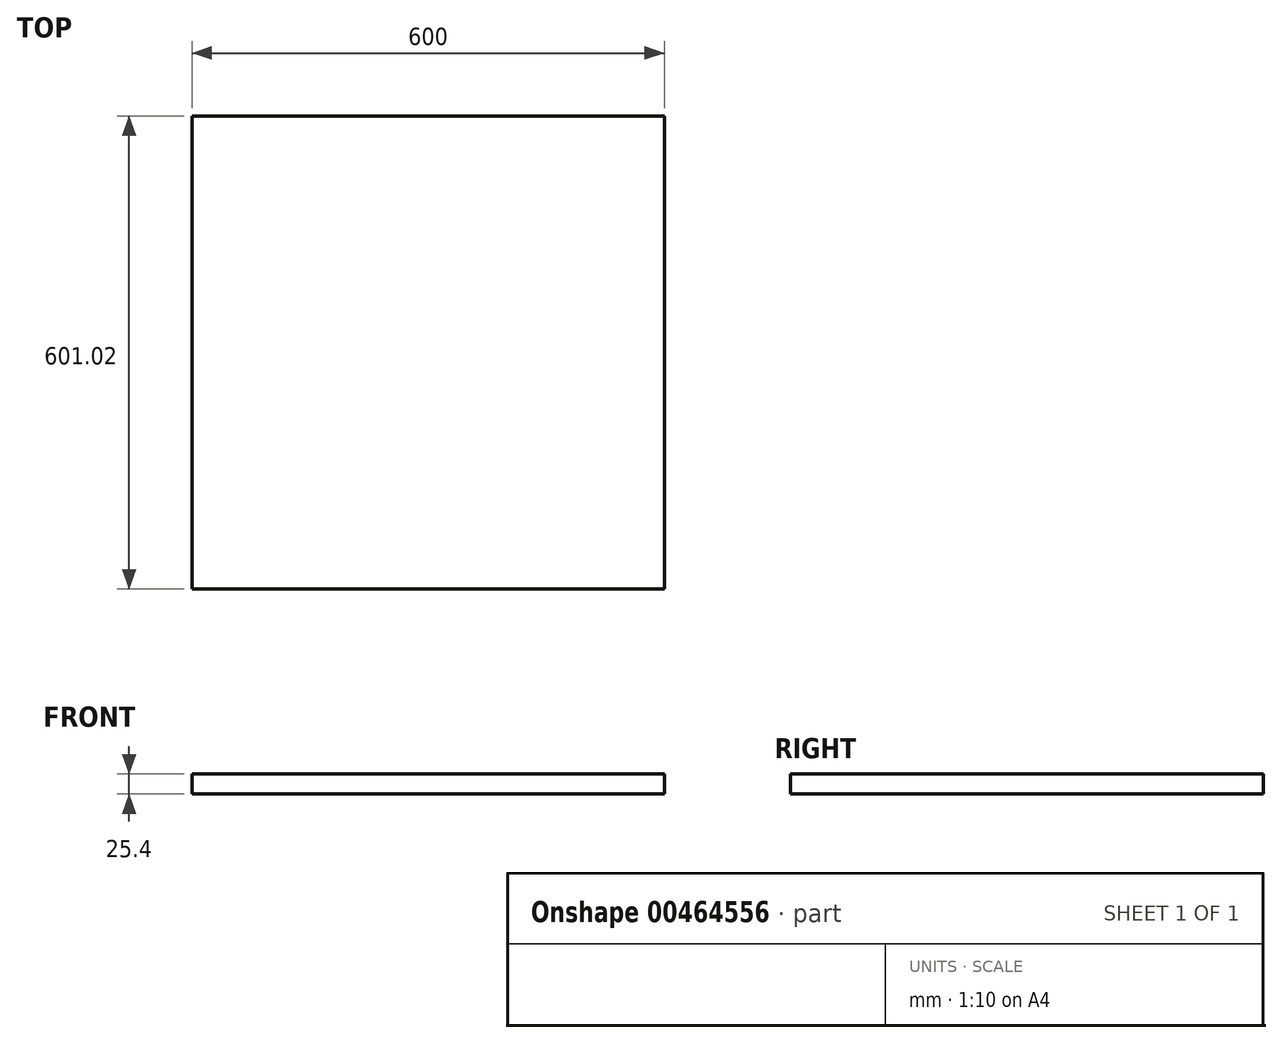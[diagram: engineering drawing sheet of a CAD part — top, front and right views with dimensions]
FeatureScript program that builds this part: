
annotation { "Feature Type Name" : "Feature", "Feature Type Description" : "" }
export const myFeature = defineFeature(function(context is Context, id is Id, definition is map)
    precondition{}
    {
        {
            var Q0;
            Q0=qCreatedBy(makeId("Top.planeOp"),FACE);
            var sketch = newSketch(context, id + "F0", { "sketchPlane" : qUnion([Q0])});
            skLineSegment(sketch, "E0.bottom", {"start": v(-300, -300.5) * mm, "end": v(300, -300.5) * mm});
            skLineSegment(sketch, "E0.top", {"start": v(-300, 300.5) * mm, "end": v(300, 300.5) * mm});
            skLineSegment(sketch, "E0.left", {"start": v(-300, -300.5) * mm, "end": v(-300, 300.5) * mm});
            skLineSegment(sketch, "E0.right", {"start": v(300, -300.5) * mm, "end": v(300, 300.5) * mm});
            skPoint(sketch, "E0.middle", {"position": v(0, 0) * mm});
            skSolve(sketch);
        }
        {
            var Q0;
            Q0=makeQuery(id+"F0.imprint","IMPRINT",FACE,{"disambiguationData":[TD([[makeQuery(id+"F0.imprint","IMPRINT",EDGE,{"derivedFrom":sQuery(id+"F0.wireOp",EDGE,"E0.bottom")}),1.0]])]});
            extrude(context, id + "F1", {"entities" : qUnion([Q0]), "depth" : 25.4 * mm});
        }
        {
            var Q0;
            Q0=makeQuery(id+"F1.opExtrude","CAP_FACE",FACE,{"disambiguationData":[OSD([sQuery(id+"F0.wireOp",EDGE,"E0.bottom"),sQuery(id+"F0.wireOp",EDGE,"E0.top"),sQuery(id+"F0.wireOp",EDGE,"E0.left"),sQuery(id+"F0.wireOp",EDGE,"E0.right")])],"isStart":true});
            var sketch = newSketch(context, id + "F2", { "sketchPlane" : qUnion([Q0])});
            skLineSegment(sketch, "E1.bottom", {"start": v(-249.2, 249.7) * mm, "end": v(-147.6, 249.7) * mm});
            skLineSegment(sketch, "E1.top", {"start": v(-249.2, 148.1) * mm, "end": v(-147.6, 148.1) * mm});
            skLineSegment(sketch, "E1.left", {"start": v(-249.2, 249.7) * mm, "end": v(-249.2, 148.1) * mm});
            skLineSegment(sketch, "E1.right", {"start": v(-147.6, 249.7) * mm, "end": v(-147.6, 148.1) * mm});
            skLineSegment(sketch, "E2.bottom", {"start": v(249.2, 249.7) * mm, "end": v(147.6, 249.7) * mm});
            skLineSegment(sketch, "E2.top", {"start": v(249.2, 148.1) * mm, "end": v(147.6, 148.1) * mm});
            skLineSegment(sketch, "E2.left", {"start": v(249.2, 249.7) * mm, "end": v(249.2, 148.1) * mm});
            skLineSegment(sketch, "E2.right", {"start": v(147.6, 249.7) * mm, "end": v(147.6, 148.1) * mm});
            skLineSegment(sketch, "E3.bottom", {"start": v(249.2, -249.7) * mm, "end": v(147.6, -249.7) * mm});
            skLineSegment(sketch, "E3.top", {"start": v(249.2, -148.1) * mm, "end": v(147.6, -148.1) * mm});
            skLineSegment(sketch, "E3.left", {"start": v(249.2, -249.7) * mm, "end": v(249.2, -148.1) * mm});
            skLineSegment(sketch, "E3.right", {"start": v(147.6, -249.7) * mm, "end": v(147.6, -148.1) * mm});
            skLineSegment(sketch, "E4.bottom", {"start": v(-249.2, -249.7) * mm, "end": v(-147.6, -249.7) * mm});
            skLineSegment(sketch, "E4.top", {"start": v(-249.2, -148.1) * mm, "end": v(-147.6, -148.1) * mm});
            skLineSegment(sketch, "E4.left", {"start": v(-249.2, -249.7) * mm, "end": v(-249.2, -148.1) * mm});
            skLineSegment(sketch, "E4.right", {"start": v(-147.6, -249.7) * mm, "end": v(-147.6, -148.1) * mm});
            skSolve(sketch);
        }
    });
